# Revit family: LIXIL - FM2-100 N - COBRA FLUSH MASTER TOILET FLUSH VALVE
name_source: partatom
category: Plumbing Fixtures
units: mm (PartAtom-declared; Revit-internal decimal feet)

## family parameters
Always vertical = Yes
Cut with Voids When Loaded = No
Enable Cutting in Views = No
Maintain Annotation Orientation = No
OmniClass Number = 23.45.00.00
OmniClass Title = Sanitary, Laundry, and Cleaning Equipment
Part Type = Normal
Room Calculation Point = No
Round Connector Dimension = Use Diameter
Shared = Yes
Work Plane-Based = No

## types (1)
- FM2-100 N
    DEPTH - 70MM - 140MM MAX = 140 mm  [stored 0.459318 ft]
    Default Elevation = 0 mm  [stored 0 ft]
    Description = Cobra Flush Master Toilet Flush Valve to detail and spec. See sanware schedule. Available from Lixil.
    HEIGHT - 125MM - 415MM MAX = 350 mm
    Hosted on lixil.co.za = https://www.lixil.co.za
    M _ FLUSH PIPE _ CHROME = M _ LIXIL - CHROME 01
    M _ FLUSH VALVE BODY = M _ LIXIL - CHROME 01
    M _ RUBBER _ BLACK _ SOFT = M _ LIXIL - RUBBER - BLACK 01
    Product Specification = Supplier: Lixil.
Product description: Exposed back entry. Non-hold open feature. With wall flange, integral vacuum breaker, and butterfly control inlet. With bent flush pipe and rubber pan connector. 1 1/4BSP female iron connection end. Recommended optimum design pressures: inlet flow pressure 30 - 300kPa for back entry WC pans: Maximum system pressure 600kPa.
Product Code: FFUUSBFM-0GT01
SKU Code: FM2-100/N
Barcode: 6002194021025
Brand: Cobra
Range: Flush Master
Category: Flush Valves
Sub-Category: Toilets
Colour: Chrome
Package Height: 80 mm
Package Width: 210 mm
Package Length: 400 mm
Package Volume: 6720000 mm³
Package Weight: 2.46 kg

Notes:
- Refer to manufacturer's and supplier's installation, maintenance and cleaning manual.
- Refer to manufacturer's and supplier's guarantees and warrantees document.

note: [stored X ft] marks values corroborated as IEEE doubles in the binary element streams (Revit-internal decimal feet)

## geometry (parser evidence)
native form markers: Sweep x14
no freeform markers — native parametric forms only
